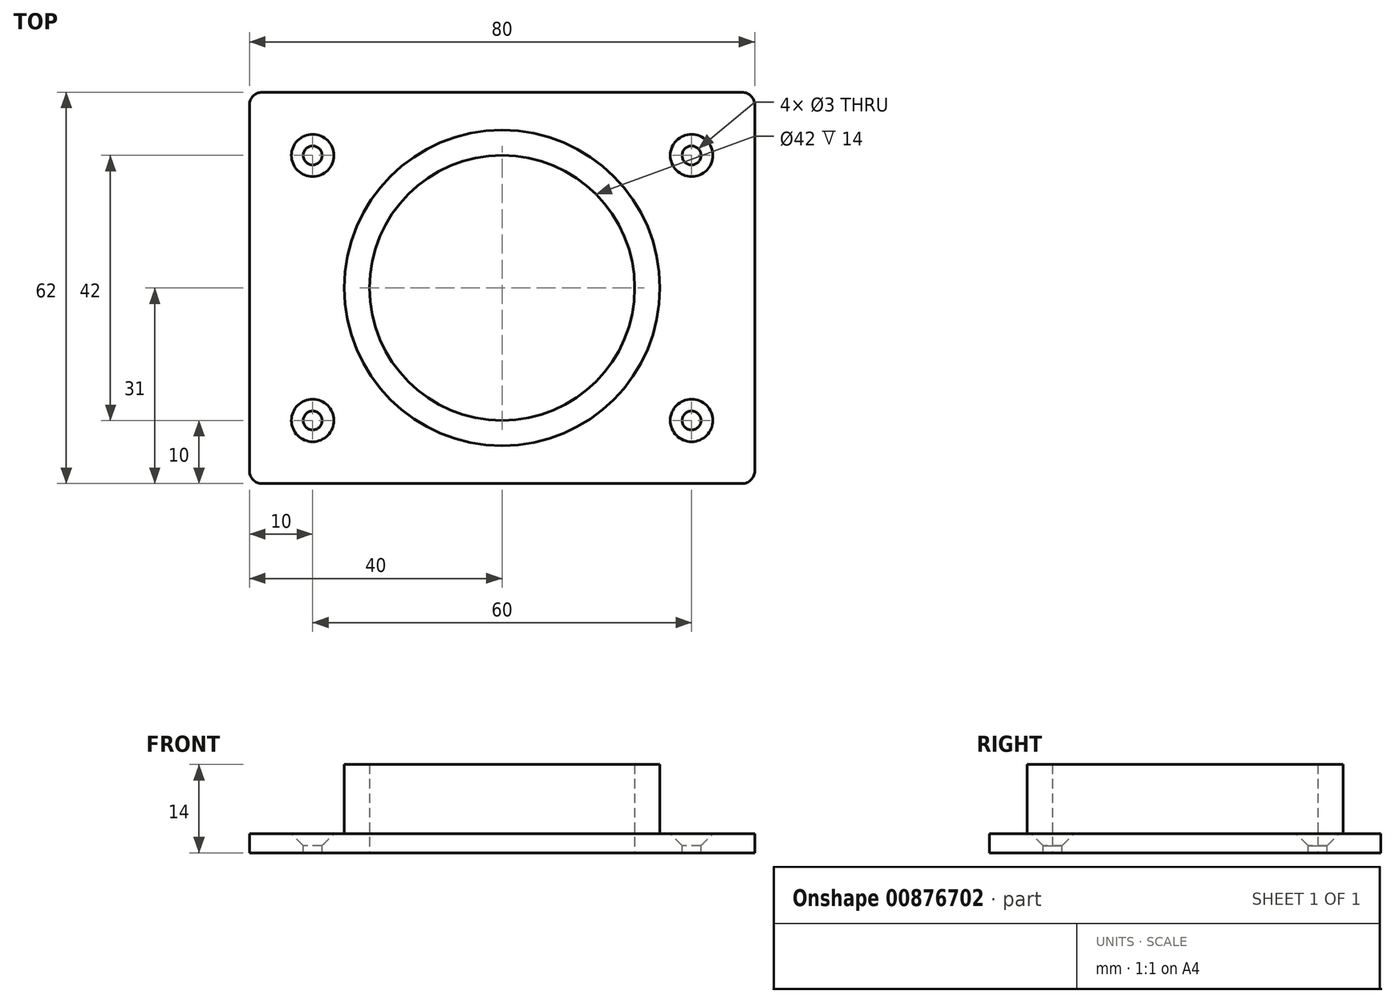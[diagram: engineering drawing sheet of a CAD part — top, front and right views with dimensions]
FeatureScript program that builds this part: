
annotation { "Feature Type Name" : "Feature", "Feature Type Description" : "" }
export const myFeature = defineFeature(function(context is Context, id is Id, definition is map)
    precondition{}
    {
        {
            var Q0;
            Q0=qCreatedBy(makeId("Top.planeOp"),FACE);
            var sketch = newSketch(context, id + "F0", { "sketchPlane" : qUnion([Q0])});
            skCircle(sketch, "E0", {"center": v(0, 0) * mm, "radius": 21 * mm});
            skCircle(sketch, "E1.0", {"center": v(0, 0) * mm, "radius": 25 * mm});
            skLineSegment(sketch, "E2.bottom", {"start": v(40, -31) * mm, "end": v(-40, -31) * mm});
            skLineSegment(sketch, "E2.top", {"start": v(40, 31) * mm, "end": v(-40, 31) * mm});
            skLineSegment(sketch, "E2.left", {"start": v(40, -31) * mm, "end": v(40, 31) * mm});
            skLineSegment(sketch, "E2.right", {"start": v(-40, -31) * mm, "end": v(-40, 31) * mm});
            skSolve(sketch);
        }
        {
            var Q0;
            Q0=makeQuery(id+"F0.imprint","IMPRINT",FACE,{"disambiguationData":[TD([[makeQuery(id+"F0.imprint","IMPRINT",EDGE,{"derivedFrom":sQuery(id+"F0.wireOp",EDGE,"E0")}),-1.0]])]});
            extrude(context, id + "F1", {"entities" : qUnion([Q0]), "depth" : 14 * mm, "offsetDistance" : 25 * mm});
        }
        {
            var Q0;
            Q0=makeQuery(id+"F0.imprint","IMPRINT",FACE,{"disambiguationData":[TD([[makeQuery(id+"F0.imprint","IMPRINT",EDGE,{"derivedFrom":sQuery(id+"F0.wireOp",EDGE,"E1.0")}),-1.0]])]});
            extrude(context, id + "F2", {"entities" : qUnion([Q0]), "operationType" : NewBodyOperationType.ADD, "depth" : 3 * mm, "offsetDistance" : 25 * mm});
        }
        {
            var Q0;
            Q0=makeQuery(id+"F2.opExtrude","SWEPT_EDGE",EDGE,{"disambiguationData":[OSD([sQuery(id+"F0.wireOp",EDGE,"E2.bottom"),sQuery(id+"F0.wireOp",EDGE,"E2.right")])]});
            var Q1;
            Q1=makeQuery(id+"F2.opExtrude","SWEPT_EDGE",EDGE,{"disambiguationData":[OSD([sQuery(id+"F0.wireOp",EDGE,"E2.bottom"),sQuery(id+"F0.wireOp",EDGE,"E2.left")])]});
            var Q2;
            Q2=makeQuery(id+"F2.opExtrude","SWEPT_EDGE",EDGE,{"disambiguationData":[OSD([sQuery(id+"F0.wireOp",EDGE,"E2.top"),sQuery(id+"F0.wireOp",EDGE,"E2.left")])]});
            var Q3;
            Q3=makeQuery(id+"F2.opExtrude","SWEPT_EDGE",EDGE,{"disambiguationData":[OSD([sQuery(id+"F0.wireOp",EDGE,"E2.top"),sQuery(id+"F0.wireOp",EDGE,"E2.right")])]});
            fillet(context, id + "F3", {"entities" : qUnion([Q0, Q1, Q2, Q3]), "radius" : 2 * mm, "tangentPropagation" : true, "allowEdgeOverflow" : false});
        }
        {
            var Q0;
            Q0=makeQuery(id+"F2.opExtrude","CAP_FACE",FACE,{"disambiguationData":[OSD([sQuery(id+"F0.wireOp",EDGE,"E1.0"),sQuery(id+"F0.wireOp",EDGE,"E2.bottom"),sQuery(id+"F0.wireOp",EDGE,"E2.top"),sQuery(id+"F0.wireOp",EDGE,"E2.left"),sQuery(id+"F0.wireOp",EDGE,"E2.right")])],"isStart":false});
            var sketch = newSketch(context, id + "F4", { "sketchPlane" : qUnion([Q0])});
            skPoint(sketch, "E3", {"position": v(-30, 21) * mm});
            skPoint(sketch, "E4", {"position": v(30, 21) * mm});
            skPoint(sketch, "E5", {"position": v(30, -21) * mm});
            skPoint(sketch, "E6", {"position": v(-30, -21) * mm});
            skSolve(sketch);
        }
        {
            var Q0;
            Q0=sQuery(id+"F4.wireOp",VERTEX,"E3");
            var Q1;
            Q1=sQuery(id+"F4.wireOp",VERTEX,"E6");
            var Q2;
            Q2=sQuery(id+"F4.wireOp",VERTEX,"E5");
            var Q3;
            Q3=sQuery(id+"F4.wireOp",VERTEX,"E4");
            var Q4;
            Q4=makeQuery(id+"F1.opExtrude","SWEPT_BODY",BODY,{"disambiguationData":[OSD([sQuery(id+"F0.wireOp",EDGE,"E0"),sQuery(id+"F0.wireOp",EDGE,"E1.0")])]});
            hole(context, id + "F5", {"style" : HoleStyle.C_SINK, "endStyle" : HoleEndStyle.THROUGH, "standardTappedOrClearance" : lookupTablePath({ "fit" : "Standard", "standard" : "ISO", "size" : "M3", "type" : "Clearance" }), "standardBlindInLast" : lookupTablePath({ "fit" : "Standard", "standard" : "ISO", "size" : "M3", "type" : "Clearance" }), "holeDiameter" : 3 * mm, "cSinkDiameter" : 6.72 * mm, "cSinkAngle" : 90 * degree, "majorDiameter" : 5 * mm, "isTappedThrough" : true, "tappedDepth" : 12 * mm, "tapClearance" : 3, "locations" : qUnion([Q0, Q1, Q2, Q3]), "scope" : qUnion([Q4])});
        }
    });
